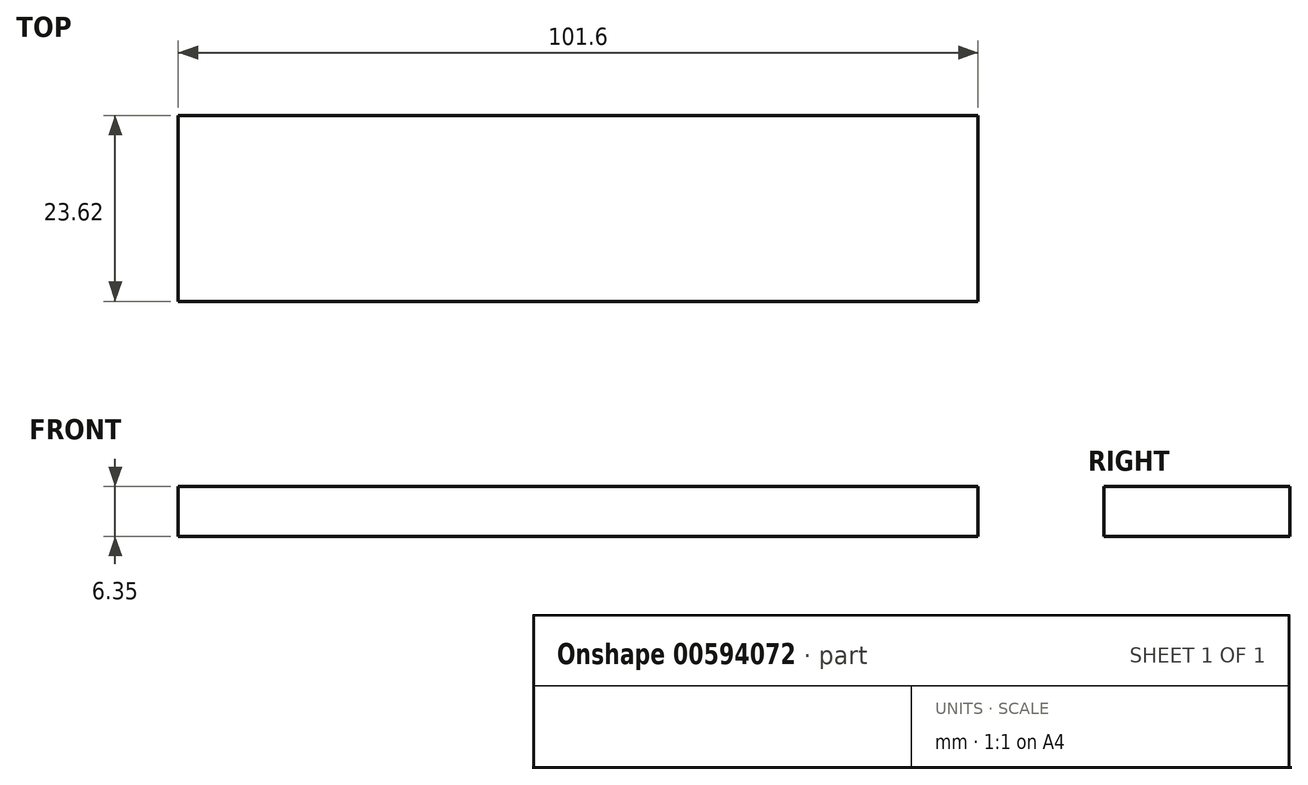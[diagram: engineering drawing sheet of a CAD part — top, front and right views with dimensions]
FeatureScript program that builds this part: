
annotation { "Feature Type Name" : "Feature", "Feature Type Description" : "" }
export const myFeature = defineFeature(function(context is Context, id is Id, definition is map)
    precondition{}
    {
        {
            var Q0;
            Q0=qCreatedBy(makeId("Top.planeOp"),FACE);
            var sketch = newSketch(context, id + "F0", { "sketchPlane" : qUnion([Q0])});
            skLineSegment(sketch, "E0.bottom", {"start": v(0, 0) * mm, "end": v(101.6, 0) * mm});
            skLineSegment(sketch, "E0.top", {"start": v(0, -23.62) * mm, "end": v(101.6, -23.62) * mm});
            skLineSegment(sketch, "E0.left", {"start": v(0, 0) * mm, "end": v(0, -23.62) * mm});
            skLineSegment(sketch, "E0.right", {"start": v(101.6, 0) * mm, "end": v(101.6, -23.62) * mm});
            skSolve(sketch);
        }
        {
            var Q0;
            Q0=makeQuery(id+"F0.imprint","IMPRINT",FACE,{"disambiguationData":[TD([[makeQuery(id+"F0.imprint","IMPRINT",EDGE,{"derivedFrom":sQuery(id+"F0.wireOp",EDGE,"E0.bottom")}),-1.0]])]});
            extrude(context, id + "F1", {"entities" : qUnion([Q0]), "depth" : 6.35 * mm, "offsetDistance" : 25.4 * mm});
        }
    });
